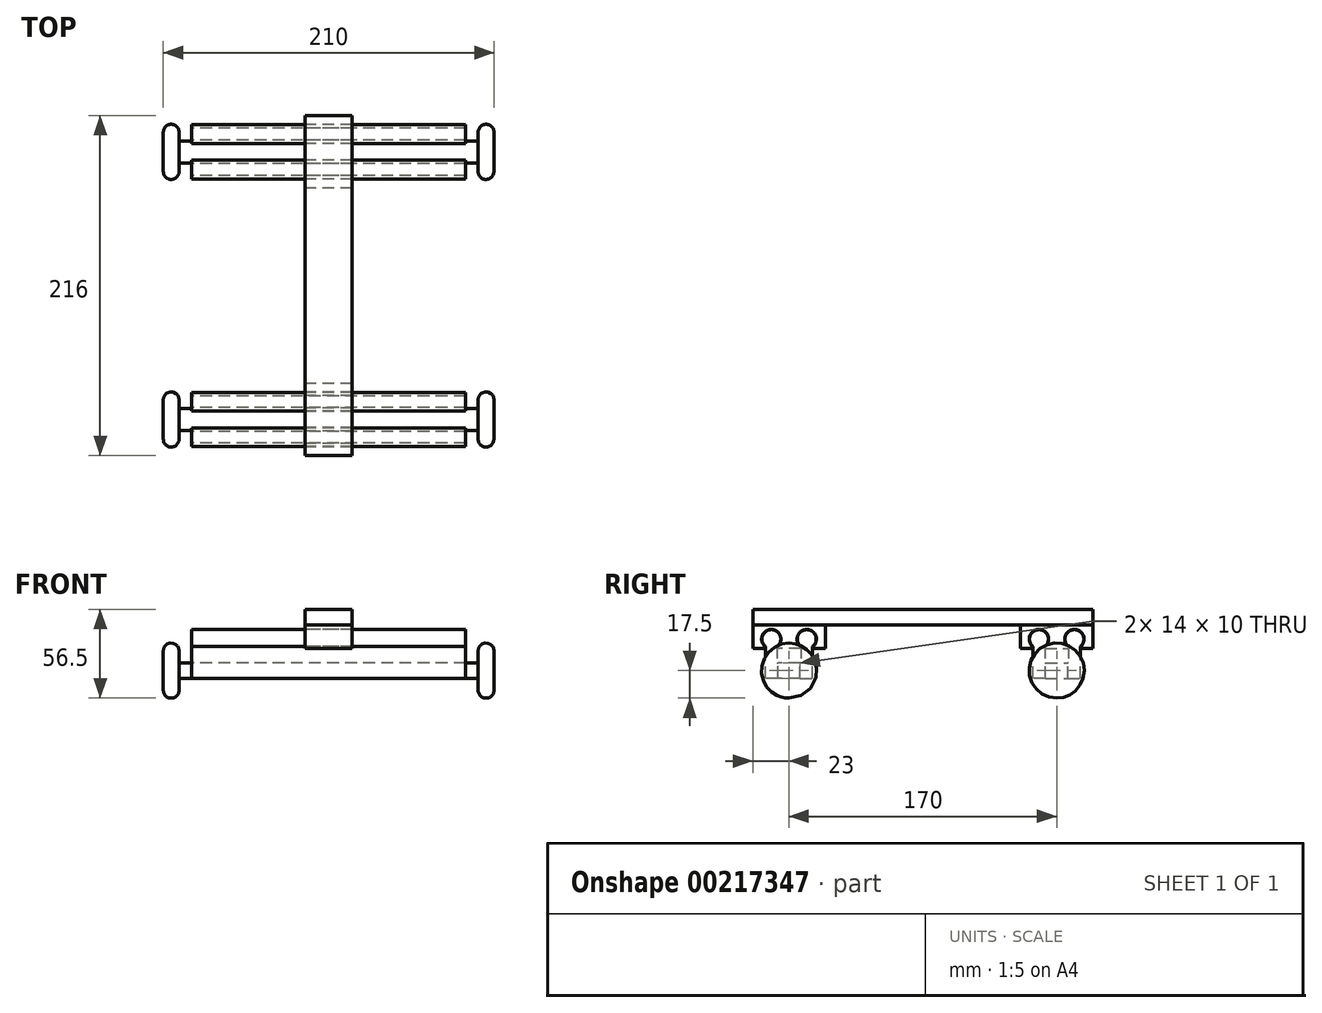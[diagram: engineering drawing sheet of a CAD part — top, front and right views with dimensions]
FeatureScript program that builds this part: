
annotation { "Feature Type Name" : "Feature", "Feature Type Description" : "" }
export const myFeature = defineFeature(function(context is Context, id is Id, definition is map)
    precondition{}
    {
        {
            var Q0;
            Q0=qCreatedBy(makeId("Front.planeOp"),FACE);
            var sketch = newSketch(context, id + "F0", { "sketchPlane" : qUnion([Q0])});
            skLineSegment(sketch, "E0.bottom", {"start": v(100, 5) * mm, "end": v(-100, 5) * mm});
            skLineSegment(sketch, "E0.top", {"start": v(100, -5) * mm, "end": v(-100, -5) * mm});
            skLineSegment(sketch, "E0.left", {"start": v(100, 5) * mm, "end": v(100, -5) * mm});
            skLineSegment(sketch, "E0.right", {"start": v(-100, 5) * mm, "end": v(-100, -5) * mm});
            skPoint(sketch, "E0.middle", {"position": v(0, 0) * mm});
            skSolve(sketch);
        }
        {
            var Q0;
            Q0=makeQuery(id+"F0.imprint","IMPRINT",FACE,{"disambiguationData":[TD([[makeQuery(id+"F0.imprint","IMPRINT",EDGE,{"derivedFrom":sQuery(id+"F0.wireOp",EDGE,"E0.bottom")}),1.0]])]});
            extrude(context, id + "F1", {"entities" : qUnion([Q0]), "endBound" : BoundingType.SYMMETRIC, "depth" : 30 * mm});
        }
        {
            var Q0;
            Q0=makeQuery(id+"F1.opExtrude","SWEPT_FACE",FACE,{"disambiguationData":[OSD([sQuery(id+"F0.wireOp",EDGE,"E0.right")])]});
            var sketch = newSketch(context, id + "F2", { "sketchPlane" : qUnion([Q0])});
            skCircle(sketch, "E1", {"center": v(0, 0) * mm, "radius": 17.5 * mm});
            skSolve(sketch);
        }
        {
            var Q0;
            Q0=makeQuery(id+"F1.opExtrude","SWEPT_FACE",FACE,{"disambiguationData":[OSD([sQuery(id+"F0.wireOp",EDGE,"E0.left")])]});
            var sketch = newSketch(context, id + "F3", { "sketchPlane" : qUnion([Q0])});
            skCircle(sketch, "E2", {"center": v(0, 0) * mm, "radius": 17.5 * mm});
            skSolve(sketch);
        }
        {
            var Q0;
            Q0=makeQuery(id+"F3.imprint","IMPRINT",FACE,{"disambiguationData":[TD([[makeQuery(id+"F3.imprint","IMPRINT",EDGE,{"derivedFrom":sQuery(id+"F3.wireOp",EDGE,"E2")}),1.0]])]});
            var Q1;
            {var subQ0=sQuery(id+"F0.wireOp",EDGE,"E0.left");Q1=makeQuery(id+"F3.imprint","IMPRINT",FACE,{"disambiguationData":[TD([[makeQuery(id+"F3.imprint","IMPRINT",EDGE,{"derivedFrom":makeQuery(id+"F1.opExtrude","CAP_EDGE",EDGE,{"disambiguationData":[OSD([subQ0])],"isStart":true})}),-1.0]])]});}
            var Q2;
            Q2=makeQuery(id+"F2.imprint","IMPRINT",FACE,{"disambiguationData":[TD([[makeQuery(id+"F2.imprint","IMPRINT",EDGE,{"derivedFrom":sQuery(id+"F2.wireOp",EDGE,"E1")}),1.0]])]});
            var Q3;
            {var subQ0=sQuery(id+"F0.wireOp",EDGE,"E0.right");Q3=makeQuery(id+"F2.imprint","IMPRINT",FACE,{"disambiguationData":[TD([[makeQuery(id+"F2.imprint","IMPRINT",EDGE,{"derivedFrom":makeQuery(id+"F1.opExtrude","CAP_EDGE",EDGE,{"disambiguationData":[OSD([subQ0])],"isStart":true})}),1.0]])]});}
            extrude(context, id + "F4", {"entities" : qUnion([Q0, Q1, Q2, Q3]), "operationType" : NewBodyOperationType.ADD, "endBound" : BoundingType.SYMMETRIC, "depth" : 10 * mm});
        }
        {
            var Q0;
            Q0=makeQuery(id+"F1.opExtrude","SWEPT_FACE",FACE,{"disambiguationData":[OSD([sQuery(id+"F0.wireOp",EDGE,"E0.bottom")])]});
            var sketch = newSketch(context, id + "F5", { "sketchPlane" : qUnion([Q0])});
            skLineSegment(sketch, "E3.bottom", {"start": v(-95, 15) * mm, "end": v(-87, 15) * mm});
            skLineSegment(sketch, "E3.top", {"start": v(-95, 7) * mm, "end": v(-87, 7) * mm});
            skLineSegment(sketch, "E3.left", {"start": v(-95, 15) * mm, "end": v(-95, 7) * mm});
            skLineSegment(sketch, "E3.right", {"start": v(-87, 15) * mm, "end": v(-87, 7) * mm});
            skLineSegment(sketch, "E4.bottom", {"start": v(-95, -15) * mm, "end": v(-87, -15) * mm});
            skLineSegment(sketch, "E4.top", {"start": v(-95, -7) * mm, "end": v(-87, -7) * mm});
            skLineSegment(sketch, "E4.left", {"start": v(-95, -15) * mm, "end": v(-95, -7) * mm});
            skLineSegment(sketch, "E4.right", {"start": v(-87, -15) * mm, "end": v(-87, -7) * mm});
            skLineSegment(sketch, "E5.bottom", {"start": v(95, 15) * mm, "end": v(87, 15) * mm});
            skLineSegment(sketch, "E5.top", {"start": v(95, 7) * mm, "end": v(87, 7) * mm});
            skLineSegment(sketch, "E5.left", {"start": v(95, 15) * mm, "end": v(95, 7) * mm});
            skLineSegment(sketch, "E5.right", {"start": v(87, 15) * mm, "end": v(87, 7) * mm});
            skLineSegment(sketch, "E6.bottom", {"start": v(95, -15) * mm, "end": v(87, -15) * mm});
            skLineSegment(sketch, "E6.top", {"start": v(95, -7) * mm, "end": v(87, -7) * mm});
            skLineSegment(sketch, "E6.left", {"start": v(95, -15) * mm, "end": v(95, -7) * mm});
            skLineSegment(sketch, "E6.right", {"start": v(87, -15) * mm, "end": v(87, -7) * mm});
            skSolve(sketch);
        }
        {
            var Q0;
            Q0=makeQuery(id+"F5.imprint","IMPRINT",FACE,{"disambiguationData":[TD([[makeQuery(id+"F5.imprint","IMPRINT",EDGE,{"derivedFrom":sQuery(id+"F5.wireOp",EDGE,"E3.bottom")}),1.0]])]});
            var Q1;
            Q1=makeQuery(id+"F5.imprint","IMPRINT",FACE,{"disambiguationData":[TD([[makeQuery(id+"F5.imprint","IMPRINT",EDGE,{"derivedFrom":sQuery(id+"F5.wireOp",EDGE,"E4.bottom")}),-1.0]])]});
            var Q2;
            Q2=makeQuery(id+"F5.imprint","IMPRINT",FACE,{"disambiguationData":[TD([[makeQuery(id+"F5.imprint","IMPRINT",EDGE,{"derivedFrom":sQuery(id+"F5.wireOp",EDGE,"E5.bottom")}),1.0]])]});
            var Q3;
            Q3=makeQuery(id+"F5.imprint","IMPRINT",FACE,{"disambiguationData":[TD([[makeQuery(id+"F5.imprint","IMPRINT",EDGE,{"derivedFrom":sQuery(id+"F5.wireOp",EDGE,"E6.bottom")}),-1.0]])]});
            extrude(context, id + "F6", {"entities" : qUnion([Q0, Q1, Q2, Q3]), "operationType" : NewBodyOperationType.REMOVE, "oppositeDirection" : true, "depth" : 25 * mm});
        }
        {
            var Q0;
            Q0=qCreatedBy(makeId("Front.planeOp"),FACE);
            var sketch = newSketch(context, id + "F7", { "sketchPlane" : qUnion([Q0])});
            skArc(sketch, "E7", {"start": v(-105, 12.5) * mm, "mid": v(-100, 17.5) * mm, "end": v(-95, 12.5) * mm});
            skLineSegment(sketch, "E8", {"start": v(-107.52, 17.5) * mm, "end": v(-92.12, 17.5) * mm, "construction": true});
            skLineSegment(sketch, "E9", {"start": v(-105, 12.5) * mm, "end": v(-105, 17.5) * mm});
            skLineSegment(sketch, "E10", {"start": v(-105, 17.5) * mm, "end": v(-95, 17.5) * mm});
            skLineSegment(sketch, "E11", {"start": v(-95, 17.5) * mm, "end": v(-95, 12.5) * mm});
            skLineSegment(sketch, "E12", {"start": v(80.22, 17.5) * mm, "end": v(116.27, 17.5) * mm, "construction": true});
            skArc(sketch, "E13", {"start": v(95, 12.5) * mm, "mid": v(100, 17.5) * mm, "end": v(105, 12.5) * mm});
            skLineSegment(sketch, "E14", {"start": v(95, 12.5) * mm, "end": v(95, 17.5) * mm});
            skLineSegment(sketch, "E15", {"start": v(95, 17.5) * mm, "end": v(105, 17.5) * mm});
            skLineSegment(sketch, "E16", {"start": v(105, 17.5) * mm, "end": v(105, 12.5) * mm});
            skSolve(sketch);
        }
        {
            var Q0;
            Q0=qCreatedBy(makeId("Front.planeOp"),FACE);
            var sketch = newSketch(context, id + "F8", { "sketchPlane" : qUnion([Q0])});
            skLineSegment(sketch, "E17", {"start": v(-131.56, 0) * mm, "end": v(119.98, 0) * mm, "construction": true});
            skSolve(sketch);
        }
        {
            var Q0;
            {var subQ0=sQuery(id+"F7.wireOp",EDGE,"E11");Q0=makeQuery(id+"F7.imprint","IMPRINT",FACE,{"disambiguationData":[TD([[makeQuery(id+"F7.imprint","IMPRINT",EDGE,{"derivedFrom":subQ0}),-1.0]])]});}
            var Q1;
            {var subQ0=sQuery(id+"F7.wireOp",EDGE,"E9");Q1=makeQuery(id+"F7.imprint","IMPRINT",FACE,{"disambiguationData":[TD([[makeQuery(id+"F7.imprint","IMPRINT",EDGE,{"derivedFrom":subQ0}),-1.0]])]});}
            var Q2;
            {var subQ0=sQuery(id+"F7.wireOp",EDGE,"E14");Q2=makeQuery(id+"F7.imprint","IMPRINT",FACE,{"disambiguationData":[TD([[makeQuery(id+"F7.imprint","IMPRINT",EDGE,{"derivedFrom":subQ0}),-1.0]])]});}
            var Q3;
            {var subQ0=sQuery(id+"F7.wireOp",EDGE,"E16");Q3=makeQuery(id+"F7.imprint","IMPRINT",FACE,{"disambiguationData":[TD([[makeQuery(id+"F7.imprint","IMPRINT",EDGE,{"derivedFrom":subQ0}),-1.0]])]});}
            var Q4;
            Q4=sQuery(id+"F8.wireOp",EDGE,"E17");
            revolve(context, id + "F9", {"operationType" : NewBodyOperationType.REMOVE, "entities" : qUnion([Q0, Q1, Q2, Q3]), "axis" : qUnion([Q4]), "revolveType" : RevolveType.FULL, "oppositeDirection" : true});
        }
        {
            var Q0;
            Q0=makeQuery(id+"F1.opExtrude","CAP_FACE",FACE,{"disambiguationData":[OSD([sQuery(id+"F0.wireOp",EDGE,"E0.bottom"),sQuery(id+"F0.wireOp",EDGE,"E0.top"),sQuery(id+"F0.wireOp",EDGE,"E0.left"),sQuery(id+"F0.wireOp",EDGE,"E0.right")])],"isStart":false});
            cPlane(context, id + "F10", {"entities" : qUnion([Q0]), "cplaneType" : CPlaneType.OFFSET, "offset" : 100 * mm, "oppositeDirection" : true, "width" : 150 * mm, "height" : 150 * mm});
        }
        {
            var Q0;
            Q0=qCreatedBy(makeId("Right.planeOp"),FACE);
            var sketch = newSketch(context, id + "F11", { "sketchPlane" : qUnion([Q0])});
            skLineSegment(sketch, "E18.bottom", {"start": v(15, 0) * mm, "end": v(-15, 0) * mm});
            skLineSegment(sketch, "E18.top", {"start": v(15, 20) * mm, "end": v(-15, 20) * mm});
            skLineSegment(sketch, "E18.left", {"start": v(15, 0) * mm, "end": v(15, 20) * mm});
            skLineSegment(sketch, "E18.right", {"start": v(-15, 0) * mm, "end": v(-15, 20) * mm});
            skLineSegment(sketch, "E19.bottom", {"start": v(7.5, 20) * mm, "end": v(-7.5, 20) * mm});
            skLineSegment(sketch, "E19.top", {"start": v(7.5, 5) * mm, "end": v(-7.5, 5) * mm});
            skLineSegment(sketch, "E19.left", {"start": v(7.5, 20) * mm, "end": v(7.5, 5) * mm});
            skLineSegment(sketch, "E19.right", {"start": v(-7.5, 20) * mm, "end": v(-7.5, 5) * mm});
            skSolve(sketch);
        }
        {
            var Q0;
            Q0=makeQuery(id+"F11.imprint","IMPRINT",FACE,{"disambiguationData":[TD([[makeQuery(id+"F11.imprint","IMPRINT",EDGE,{"derivedFrom":sQuery(id+"F11.wireOp",EDGE,"E18.bottom")}),-1.0]])]});
            extrude(context, id + "F12", {"entities" : qUnion([Q0]), "operationType" : NewBodyOperationType.ADD, "endBound" : BoundingType.SYMMETRIC, "depth" : (200 - 16 - 10) * mm});
        }
        {
            var Q0;
            Q0=makeQuery(id+"F12.boolean.opBoolean","MERGE",FACE,{"derivedFrom":[makeQuery(id+"F6.boolean.opBoolean","COPY",FACE,{"derivedFrom":makeQuery(id+"F6.opExtrude","SWEPT_FACE",FACE,{"disambiguationData":[OSD([sQuery(id+"F5.wireOp",EDGE,"E4.right")])]})}),makeQuery(id+"F12.opExtrude","CAP_FACE",FACE,{"disambiguationData":[OSD([sQuery(id+"F11.wireOp",EDGE,"E18.bottom"),sQuery(id+"F11.wireOp",EDGE,"E18.top"),sQuery(id+"F11.wireOp",EDGE,"E18.left"),sQuery(id+"F11.wireOp",EDGE,"E18.right"),sQuery(id+"F11.wireOp",EDGE,"E19.top"),sQuery(id+"F11.wireOp",EDGE,"E19.left"),sQuery(id+"F11.wireOp",EDGE,"E19.right")])],"isStart":true})]});
            var sketch = newSketch(context, id + "F13", { "sketchPlane" : qUnion([Q0])});
            skCircle(sketch, "E20", {"center": v(-11.25, 20) * mm, "radius": 6 * mm});
            skCircle(sketch, "E21", {"center": v(11.25, 20) * mm, "radius": 6 * mm});
            skSolve(sketch);
        }
        {
            var Q0;
            Q0=makeQuery(id+"F13.imprint","IMPRINT",FACE,{"disambiguationData":[TD([[makeQuery(id+"F13.imprint","IMPRINT",EDGE,{"derivedFrom":sQuery(id+"F13.wireOp",EDGE,"E20")}),1.0]])]});
            var Q1;
            {var subQ4=sQuery(id+"F11.wireOp",EDGE,"E18.right");var subQ7=sQuery(id+"F11.wireOp",EDGE,"E18.top");var subQ8=makeQuery(id+"F12.opExtrude","CAP_EDGE",EDGE,{"disambiguationData":[OSD([subQ7]),TDD([makeQuery(id+"F11.imprint","IMPRINT",EDGE,{"disambiguationData":[TD([[makeQuery(id+"F11.imprint","INTERSECT",VERTEX,{"derivedFrom":[subQ7,subQ4]}),1.0]])],"derivedFrom":subQ7})])],"isStart":true});Q1=makeQuery(id+"F13.imprint","IMPRINT",FACE,{"disambiguationData":[TD([[makeQuery(id+"F13.imprint","IMPRINT",EDGE,{"derivedFrom":subQ8}),1.0]])]});}
            var Q2;
            Q2=makeQuery(id+"F12.boolean.opBoolean","MERGE",FACE,{"derivedFrom":[makeQuery(id+"F6.boolean.opBoolean","COPY",FACE,{"derivedFrom":makeQuery(id+"F6.opExtrude","SWEPT_FACE",FACE,{"disambiguationData":[OSD([sQuery(id+"F5.wireOp",EDGE,"E6.right")])]})}),makeQuery(id+"F12.opExtrude","CAP_FACE",FACE,{"disambiguationData":[OSD([sQuery(id+"F11.wireOp",EDGE,"E18.bottom"),sQuery(id+"F11.wireOp",EDGE,"E18.top"),sQuery(id+"F11.wireOp",EDGE,"E18.left"),sQuery(id+"F11.wireOp",EDGE,"E18.right"),sQuery(id+"F11.wireOp",EDGE,"E19.top"),sQuery(id+"F11.wireOp",EDGE,"E19.left"),sQuery(id+"F11.wireOp",EDGE,"E19.right")])],"isStart":false})]});
            extrude(context, id + "F14", {"entities" : qUnion([Q0, Q1]), "operationType" : NewBodyOperationType.ADD, "endBound" : BoundingType.UP_TO_SURFACE, "oppositeDirection" : true, "endBoundEntityFace" : qUnion([Q2]), "depth" : 25 * mm});
        }
        {
            var Q0;
            Q0=qCreatedBy(makeId("Right.planeOp"),FACE);
            var sketch = newSketch(context, id + "F15", { "sketchPlane" : qUnion([Q0])});
            skLineSegment(sketch, "E22.bottom", {"start": v(23, 29) * mm, "end": v(-23, 29) * mm});
            skLineSegment(sketch, "E22.top", {"start": v(23, 14) * mm, "end": v(-23, 14) * mm});
            skLineSegment(sketch, "E22.left", {"start": v(23, 29) * mm, "end": v(23, 14) * mm});
            skLineSegment(sketch, "E22.right", {"start": v(-23, 29) * mm, "end": v(-23, 14) * mm});
            skLineSegment(sketch, "E23", {"start": v(38.02, 20) * mm, "end": v(-53.95, 20) * mm, "construction": true});
            skLineSegment(sketch, "E24", {"start": v(11.25, 47.8) * mm, "end": v(11.25, -27.15) * mm, "construction": true});
            skLineSegment(sketch, "E25", {"start": v(-11.25, 48.92) * mm, "end": v(-11.25, 7.51) * mm, "construction": true});
            skArc(sketch, "E26", {"start": v(15.1, 15.24) * mm, "mid": v(11.25, 26.13) * mm, "end": v(7.4, 15.24) * mm});
            skArc(sketch, "E27", {"start": v(-7.4, 15.24) * mm, "mid": v(-11.25, 26.13) * mm, "end": v(-15.1, 15.24) * mm});
            skLineSegment(sketch, "E28", {"start": v(15.1, 15.24) * mm, "end": v(15.1, 14) * mm});
            skLineSegment(sketch, "E29.MirrorCS", {"start": v(7.4, 15.24) * mm, "end": v(7.4, 14) * mm});
            skLineSegment(sketch, "E30", {"start": v(-15.1, 15.24) * mm, "end": v(-15.1, 14) * mm});
            skLineSegment(sketch, "E31.MirrorCS", {"start": v(-7.4, 15.24) * mm, "end": v(-7.4, 14) * mm});
            skSolve(sketch);
        }
        {
            var Q0;
            Q0=makeQuery(id+"F15.imprint","IMPRINT",FACE,{"disambiguationData":[TD([[makeQuery(id+"F15.imprint","IMPRINT",EDGE,{"derivedFrom":sQuery(id+"F15.wireOp",EDGE,"E22.bottom")}),1.0]])]});
            extrude(context, id + "F16", {"entities" : qUnion([Q0]), "endBound" : BoundingType.SYMMETRIC, "depth" : 30 * mm});
        }
        {
            var Q0;
            Q0=makeQuery(id+"F1.opExtrude","SWEPT_BODY",BODY,{"disambiguationData":[OSD([sQuery(id+"F0.wireOp",EDGE,"E0.bottom"),sQuery(id+"F0.wireOp",EDGE,"E0.top"),sQuery(id+"F0.wireOp",EDGE,"E0.left"),sQuery(id+"F0.wireOp",EDGE,"E0.right")])]});
            var Q1;
            Q1=makeQuery(id+"F16.opExtrude","SWEPT_BODY",BODY,{"disambiguationData":[OSD([sQuery(id+"F15.wireOp",EDGE,"E22.bottom"),sQuery(id+"F15.wireOp",EDGE,"E22.top"),sQuery(id+"F15.wireOp",EDGE,"E22.left"),sQuery(id+"F15.wireOp",EDGE,"E22.right"),sQuery(id+"F15.wireOp",EDGE,"E26"),sQuery(id+"F15.wireOp",EDGE,"E27"),sQuery(id+"F15.wireOp",EDGE,"E28"),sQuery(id+"F15.wireOp",EDGE,"E29.MirrorCS"),sQuery(id+"F15.wireOp",EDGE,"E30"),sQuery(id+"F15.wireOp",EDGE,"E31.MirrorCS")])]});
            var Q2;
            Q2=qCreatedBy(id+"F10.planeOp",FACE);
            mirror(context, id + "F17", {"entities" : qUnion([Q0, Q1]), "mirrorPlane" : qUnion([Q2])});
        }
        {
            var Q0;
            Q0=makeQuery(id+"F17.opPattern","COPY",FACE,{"derivedFrom":makeQuery(id+"F16.opExtrude","SWEPT_FACE",FACE,{"disambiguationData":[OSD([sQuery(id+"F15.wireOp",EDGE,"E22.bottom")])]}),"instanceName":"1"});
            var sketch = newSketch(context, id + "F18", { "sketchPlane" : qUnion([Q0])});
            skLineSegment(sketch, "E32.bottom", {"start": v(-15, -23) * mm, "end": v(15, -23) * mm});
            skLineSegment(sketch, "E32.top", {"start": v(-15, 193) * mm, "end": v(15, 193) * mm});
            skLineSegment(sketch, "E32.left", {"start": v(-15, -23) * mm, "end": v(-15, 193) * mm});
            skLineSegment(sketch, "E32.right", {"start": v(15, -23) * mm, "end": v(15, 193) * mm});
            skSolve(sketch);
        }
        {
            var Q0;
            {var subQ0=sQuery(id+"F18.wireOp",EDGE,"E32.bottom");Q0=makeQuery(id+"F18.imprint","IMPRINT",FACE,{"disambiguationData":[TD([[makeQuery(id+"F18.imprint","IMPRINT",EDGE,{"derivedFrom":subQ0}),1.0]])]});}
            var Q1;
            {var subQ0=sQuery(id+"F18.wireOp",EDGE,"E32.top");Q1=makeQuery(id+"F18.imprint","IMPRINT",FACE,{"disambiguationData":[TD([[makeQuery(id+"F18.imprint","IMPRINT",EDGE,{"derivedFrom":subQ0}),1.0]])]});}
            extrude(context, id + "F19", {"entities" : qUnion([Q0, Q1]), "depth" : 10 * mm});
        }
    });
